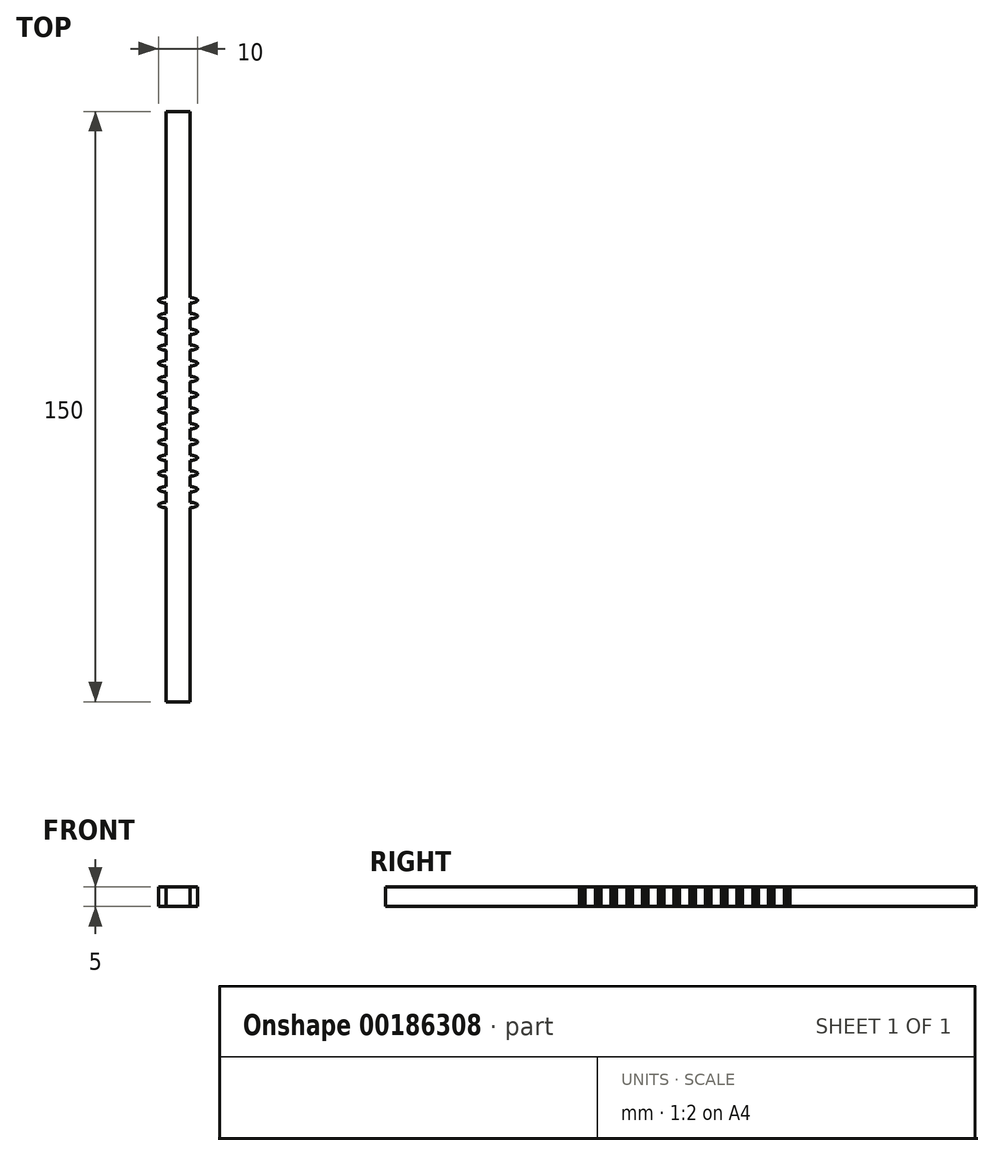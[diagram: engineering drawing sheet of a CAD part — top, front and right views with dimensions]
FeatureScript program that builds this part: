
annotation { "Feature Type Name" : "Feature", "Feature Type Description" : "" }
export const myFeature = defineFeature(function(context is Context, id is Id, definition is map)
    precondition{}
    {
        {
            var Q0;
            Q0=qCreatedBy(makeId("Top.planeOp"),FACE);
            var sketch = newSketch(context, id + "F0", { "sketchPlane" : qUnion([Q0])});
            skLineSegment(sketch, "E0.bottom", {"start": v(0, 75) * mm, "end": v(3, 75) * mm});
            skLineSegment(sketch, "E0.top", {"start": v(0, -75) * mm, "end": v(3, -75) * mm});
            skLineSegment(sketch, "E0.left", {"start": v(0, 75) * mm, "end": v(0, -75) * mm});
            skLineSegment(sketch, "E0.right", {"start": v(3, 75) * mm, "end": v(3, -75) * mm});
            skLineSegment(sketch, "E1", {"start": v(0, 27) * mm, "end": v(3, 27) * mm, "construction": true});
            skArc(sketch, "E2", {"start": v(3, 27.69) * mm, "mid": v(4.04, 27.55) * mm, "end": v(5, 27.15) * mm});
            skLineSegment(sketch, "E3", {"start": v(5, 27.15) * mm, "end": v(5, 27) * mm});
            skArc(sketch, "E4.MirrorCS", {"start": v(3, 26.31) * mm, "mid": v(4.04, 26.45) * mm, "end": v(5, 26.85) * mm});
            skLineSegment(sketch, "E5.MirrorCS", {"start": v(5, 26.85) * mm, "end": v(5, 27) * mm});
            skArc(sketch, "E6.1.0.0", {"start": v(3, 23.69) * mm, "mid": v(4.04, 23.55) * mm, "end": v(5, 23.15) * mm});
            skLineSegment(sketch, "E6.1.0.1", {"start": v(5, 23.15) * mm, "end": v(5, 23) * mm});
            skLineSegment(sketch, "E6.1.0.2", {"start": v(5, 22.85) * mm, "end": v(5, 23) * mm});
            skArc(sketch, "E6.1.0.3", {"start": v(3, 22.31) * mm, "mid": v(4.04, 22.45) * mm, "end": v(5, 22.85) * mm});
            skArc(sketch, "E6.2.0.0", {"start": v(3, 19.69) * mm, "mid": v(4.04, 19.55) * mm, "end": v(5, 19.15) * mm});
            skLineSegment(sketch, "E6.2.0.1", {"start": v(5, 19.15) * mm, "end": v(5, 19) * mm});
            skLineSegment(sketch, "E6.2.0.2", {"start": v(5, 18.85) * mm, "end": v(5, 19) * mm});
            skArc(sketch, "E6.2.0.3", {"start": v(3, 18.31) * mm, "mid": v(4.04, 18.45) * mm, "end": v(5, 18.85) * mm});
            skLineSegment(sketch, "E6.direction1", {"start": v(3, 23.69) * mm, "end": v(3, 19.69) * mm, "construction": true});
            skArc(sketch, "E7.0.3.0", {"start": v(3, 15.69) * mm, "mid": v(4.04, 15.55) * mm, "end": v(5, 15.15) * mm});
            skLineSegment(sketch, "E7.4.3.0", {"start": v(5, 15.15) * mm, "end": v(5, 15) * mm});
            skLineSegment(sketch, "E7.7.3.0", {"start": v(5, 14.85) * mm, "end": v(5, 15) * mm});
            skArc(sketch, "E7.10.3.0", {"start": v(3, 14.31) * mm, "mid": v(4.04, 14.45) * mm, "end": v(5, 14.85) * mm});
            skArc(sketch, "E7.0.4.0", {"start": v(3, 11.69) * mm, "mid": v(4.04, 11.55) * mm, "end": v(5, 11.15) * mm});
            skLineSegment(sketch, "E7.4.4.0", {"start": v(5, 11.15) * mm, "end": v(5, 11) * mm});
            skLineSegment(sketch, "E7.7.4.0", {"start": v(5, 10.85) * mm, "end": v(5, 11) * mm});
            skArc(sketch, "E7.10.4.0", {"start": v(3, 10.31) * mm, "mid": v(4.04, 10.45) * mm, "end": v(5, 10.85) * mm});
            skArc(sketch, "E7.0.5.0", {"start": v(3, 7.69) * mm, "mid": v(4.04, 7.55) * mm, "end": v(5, 7.15) * mm});
            skLineSegment(sketch, "E7.4.5.0", {"start": v(5, 7.15) * mm, "end": v(5, 7) * mm});
            skLineSegment(sketch, "E7.7.5.0", {"start": v(5, 6.85) * mm, "end": v(5, 7) * mm});
            skArc(sketch, "E7.10.5.0", {"start": v(3, 6.31) * mm, "mid": v(4.04, 6.45) * mm, "end": v(5, 6.85) * mm});
            skArc(sketch, "E7.0.6.0", {"start": v(3, 3.69) * mm, "mid": v(4.04, 3.55) * mm, "end": v(5, 3.15) * mm});
            skLineSegment(sketch, "E7.4.6.0", {"start": v(5, 3.15) * mm, "end": v(5, 3) * mm});
            skLineSegment(sketch, "E7.7.6.0", {"start": v(5, 2.85) * mm, "end": v(5, 3) * mm});
            skArc(sketch, "E7.10.6.0", {"start": v(3, 2.31) * mm, "mid": v(4.04, 2.45) * mm, "end": v(5, 2.85) * mm});
            skArc(sketch, "E7.0.7.0", {"start": v(3, -0.31) * mm, "mid": v(4.04, -0.45) * mm, "end": v(5, -0.85) * mm});
            skLineSegment(sketch, "E7.4.7.0", {"start": v(5, -0.85) * mm, "end": v(5, -1) * mm});
            skLineSegment(sketch, "E7.7.7.0", {"start": v(5, -1.15) * mm, "end": v(5, -1) * mm});
            skArc(sketch, "E7.10.7.0", {"start": v(3, -1.69) * mm, "mid": v(4.04, -1.55) * mm, "end": v(5, -1.15) * mm});
            skArc(sketch, "E7.0.8.0", {"start": v(3, -4.31) * mm, "mid": v(4.04, -4.45) * mm, "end": v(5, -4.85) * mm});
            skLineSegment(sketch, "E7.4.8.0", {"start": v(5, -4.85) * mm, "end": v(5, -5) * mm});
            skLineSegment(sketch, "E7.7.8.0", {"start": v(5, -5.15) * mm, "end": v(5, -5) * mm});
            skArc(sketch, "E7.10.8.0", {"start": v(3, -5.69) * mm, "mid": v(4.04, -5.55) * mm, "end": v(5, -5.15) * mm});
            skArc(sketch, "E7.0.9.0", {"start": v(3, -8.31) * mm, "mid": v(4.04, -8.45) * mm, "end": v(5, -8.85) * mm});
            skLineSegment(sketch, "E7.4.9.0", {"start": v(5, -8.85) * mm, "end": v(5, -9) * mm});
            skLineSegment(sketch, "E7.7.9.0", {"start": v(5, -9.15) * mm, "end": v(5, -9) * mm});
            skArc(sketch, "E7.10.9.0", {"start": v(3, -9.69) * mm, "mid": v(4.04, -9.55) * mm, "end": v(5, -9.15) * mm});
            skArc(sketch, "E7.0.10.0", {"start": v(3, -12.31) * mm, "mid": v(4.04, -12.45) * mm, "end": v(5, -12.85) * mm});
            skLineSegment(sketch, "E7.4.10.0", {"start": v(5, -12.85) * mm, "end": v(5, -13) * mm});
            skLineSegment(sketch, "E7.7.10.0", {"start": v(5, -13.15) * mm, "end": v(5, -13) * mm});
            skArc(sketch, "E7.10.10.0", {"start": v(3, -13.69) * mm, "mid": v(4.04, -13.55) * mm, "end": v(5, -13.15) * mm});
            skArc(sketch, "E7.0.11.0", {"start": v(3, -16.31) * mm, "mid": v(4.04, -16.45) * mm, "end": v(5, -16.85) * mm});
            skLineSegment(sketch, "E7.4.11.0", {"start": v(5, -16.85) * mm, "end": v(5, -17) * mm});
            skLineSegment(sketch, "E7.7.11.0", {"start": v(5, -17.15) * mm, "end": v(5, -17) * mm});
            skArc(sketch, "E7.10.11.0", {"start": v(3, -17.69) * mm, "mid": v(4.04, -17.55) * mm, "end": v(5, -17.15) * mm});
            skArc(sketch, "E7.0.12.0", {"start": v(3, -20.31) * mm, "mid": v(4.04, -20.45) * mm, "end": v(5, -20.85) * mm});
            skLineSegment(sketch, "E7.4.12.0", {"start": v(5, -20.85) * mm, "end": v(5, -21) * mm});
            skLineSegment(sketch, "E7.7.12.0", {"start": v(5, -21.15) * mm, "end": v(5, -21) * mm});
            skArc(sketch, "E7.10.12.0", {"start": v(3, -21.69) * mm, "mid": v(4.04, -21.55) * mm, "end": v(5, -21.15) * mm});
            skArc(sketch, "E7.0.13.0", {"start": v(3, -24.31) * mm, "mid": v(4.04, -24.45) * mm, "end": v(5, -24.85) * mm});
            skLineSegment(sketch, "E7.4.13.0", {"start": v(5, -24.85) * mm, "end": v(5, -25) * mm});
            skLineSegment(sketch, "E7.7.13.0", {"start": v(5, -25.15) * mm, "end": v(5, -25) * mm});
            skArc(sketch, "E7.10.13.0", {"start": v(3, -25.69) * mm, "mid": v(4.04, -25.55) * mm, "end": v(5, -25.15) * mm});
            skSolve(sketch);
        }
        {
            var Q0;
            Q0=qSketchRegion(id+"F0",true);
            extrude(context, id + "F1", {"entities" : qUnion([Q0]), "depth" : 5 * mm});
        }
        {
            var Q0;
            Q0=makeQuery(id+"F1.opExtrude","SWEPT_BODY",BODY,{"disambiguationData":[OSD([sQuery(id+"F0.wireOp",EDGE,"E0.bottom"),sQuery(id+"F0.wireOp",EDGE,"E0.top"),sQuery(id+"F0.wireOp",EDGE,"E0.left"),sQuery(id+"F0.wireOp",EDGE,"E0.right"),sQuery(id+"F0.wireOp",EDGE,"E2"),sQuery(id+"F0.wireOp",EDGE,"E3"),sQuery(id+"F0.wireOp",EDGE,"E4.MirrorCS"),sQuery(id+"F0.wireOp",EDGE,"E5.MirrorCS"),sQuery(id+"F0.wireOp",EDGE,"E6.1.0.0"),sQuery(id+"F0.wireOp",EDGE,"E6.1.0.1"),sQuery(id+"F0.wireOp",EDGE,"E6.1.0.2"),sQuery(id+"F0.wireOp",EDGE,"E6.1.0.3"),sQuery(id+"F0.wireOp",EDGE,"E6.2.0.0"),sQuery(id+"F0.wireOp",EDGE,"E6.2.0.1"),sQuery(id+"F0.wireOp",EDGE,"E6.2.0.2"),sQuery(id+"F0.wireOp",EDGE,"E6.2.0.3"),sQuery(id+"F0.wireOp",EDGE,"E7.0.3.0"),sQuery(id+"F0.wireOp",EDGE,"E7.4.3.0"),sQuery(id+"F0.wireOp",EDGE,"E7.7.3.0"),sQuery(id+"F0.wireOp",EDGE,"E7.10.3.0"),sQuery(id+"F0.wireOp",EDGE,"E7.0.4.0"),sQuery(id+"F0.wireOp",EDGE,"E7.4.4.0"),sQuery(id+"F0.wireOp",EDGE,"E7.7.4.0"),sQuery(id+"F0.wireOp",EDGE,"E7.10.4.0"),sQuery(id+"F0.wireOp",EDGE,"E7.0.5.0"),sQuery(id+"F0.wireOp",EDGE,"E7.4.5.0"),sQuery(id+"F0.wireOp",EDGE,"E7.7.5.0"),sQuery(id+"F0.wireOp",EDGE,"E7.10.5.0"),sQuery(id+"F0.wireOp",EDGE,"E7.0.6.0"),sQuery(id+"F0.wireOp",EDGE,"E7.4.6.0"),sQuery(id+"F0.wireOp",EDGE,"E7.7.6.0"),sQuery(id+"F0.wireOp",EDGE,"E7.10.6.0"),sQuery(id+"F0.wireOp",EDGE,"E7.0.7.0"),sQuery(id+"F0.wireOp",EDGE,"E7.4.7.0"),sQuery(id+"F0.wireOp",EDGE,"E7.7.7.0"),sQuery(id+"F0.wireOp",EDGE,"E7.10.7.0"),sQuery(id+"F0.wireOp",EDGE,"E7.0.8.0"),sQuery(id+"F0.wireOp",EDGE,"E7.4.8.0"),sQuery(id+"F0.wireOp",EDGE,"E7.7.8.0"),sQuery(id+"F0.wireOp",EDGE,"E7.10.8.0"),sQuery(id+"F0.wireOp",EDGE,"E7.0.9.0"),sQuery(id+"F0.wireOp",EDGE,"E7.4.9.0"),sQuery(id+"F0.wireOp",EDGE,"E7.7.9.0"),sQuery(id+"F0.wireOp",EDGE,"E7.10.9.0"),sQuery(id+"F0.wireOp",EDGE,"E7.0.10.0"),sQuery(id+"F0.wireOp",EDGE,"E7.4.10.0"),sQuery(id+"F0.wireOp",EDGE,"E7.7.10.0"),sQuery(id+"F0.wireOp",EDGE,"E7.10.10.0"),sQuery(id+"F0.wireOp",EDGE,"E7.0.11.0"),sQuery(id+"F0.wireOp",EDGE,"E7.4.11.0"),sQuery(id+"F0.wireOp",EDGE,"E7.7.11.0"),sQuery(id+"F0.wireOp",EDGE,"E7.10.11.0"),sQuery(id+"F0.wireOp",EDGE,"E7.0.12.0"),sQuery(id+"F0.wireOp",EDGE,"E7.4.12.0"),sQuery(id+"F0.wireOp",EDGE,"E7.7.12.0"),sQuery(id+"F0.wireOp",EDGE,"E7.10.12.0"),sQuery(id+"F0.wireOp",EDGE,"E7.0.13.0"),sQuery(id+"F0.wireOp",EDGE,"E7.4.13.0"),sQuery(id+"F0.wireOp",EDGE,"E7.7.13.0"),sQuery(id+"F0.wireOp",EDGE,"E7.10.13.0"),sQuery(id+"F0.wireOp",EDGE,"E7.0.14.0"),sQuery(id+"F0.wireOp",EDGE,"E7.4.14.0"),sQuery(id+"F0.wireOp",EDGE,"E7.7.14.0"),sQuery(id+"F0.wireOp",EDGE,"E7.10.14.0"),sQuery(id+"F0.wireOp",EDGE,"E7.0.15.0"),sQuery(id+"F0.wireOp",EDGE,"E7.4.15.0"),sQuery(id+"F0.wireOp",EDGE,"E7.7.15.0"),sQuery(id+"F0.wireOp",EDGE,"E7.10.15.0")])]});
            var Q1;
            Q1=makeQuery(id+"F1.opExtrude","SWEPT_FACE",FACE,{"disambiguationData":[OSD([sQuery(id+"F0.wireOp",EDGE,"E0.left")])]});
            mirror(context, id + "F2", {"operationType" : NewBodyOperationType.ADD, "entities" : qUnion([Q0]), "mirrorPlane" : qUnion([Q1])});
        }
    });
